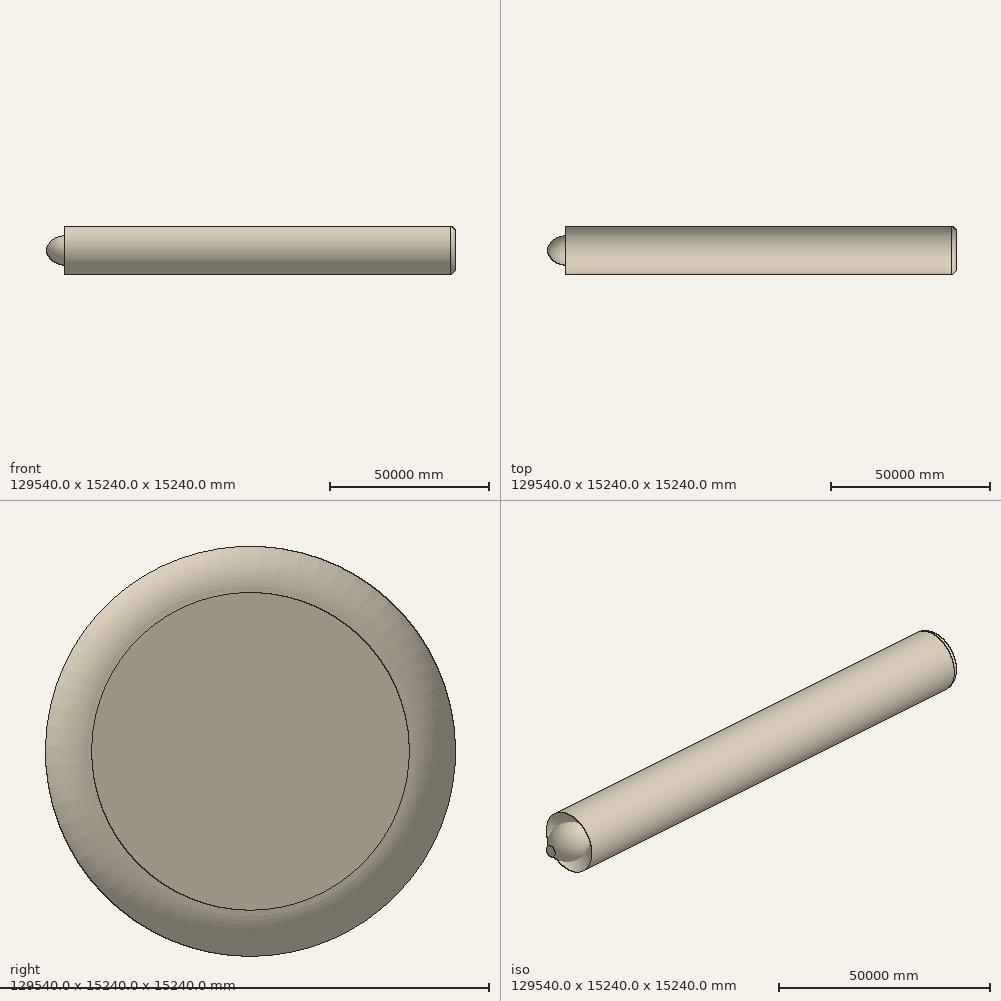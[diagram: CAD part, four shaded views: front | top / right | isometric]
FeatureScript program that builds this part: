
annotation { "Feature Type Name" : "Feature", "Feature Type Description" : "" }
export const myFeature = defineFeature(function(context is Context, id is Id, definition is map)
    precondition{}
    {
        {
            var Q0;
            Q0=qCreatedBy(makeId("Right.planeOp"),FACE);
            var sketch = newSketch(context, id + "F0", { "sketchPlane" : qUnion([Q0])});
            skCircle(sketch, "E0", {"center": v(0, 0) * mm, "radius": 7620 * mm});
            skSolve(sketch);
        }
        {
            var Q0;
            Q0=makeQuery(id+"F0.imprint","IMPRINT",FACE,{"disambiguationData":[TD([[makeQuery(id+"F0.imprint","IMPRINT",EDGE,{"derivedFrom":sQuery(id+"F0.wireOp",EDGE,"E0")}),1.0]])]});
            extrude(context, id + "F1", {"entities" : qUnion([Q0]), "endBound" : BoundingType.SYMMETRIC, "depth" : 129540 * mm, "offsetDistance" : 25.4 * mm});
        }
        {
            var Q0;
            Q0=makeQuery(id+"F1.opExtrude","CAP_EDGE",EDGE,{"disambiguationData":[OSD([sQuery(id+"F0.wireOp",EDGE,"E0")])],"isStart":true});
            fillet(context, id + "F2", {"entities" : qUnion([Q0]), "radius" : 6132.1 * mm, "tangentPropagation" : true, "allowEdgeOverflow" : false});
        }
        {
            var Q0;
            Q0=makeQuery(id+"F1.opExtrude","CAP_FACE",FACE,{"disambiguationData":[OSD([sQuery(id+"F0.wireOp",EDGE,"E0")])],"isStart":false});
            fillet(context, id + "F3", {"entities" : qUnion([Q0]), "radius" : 1717 * mm, "tangentPropagation" : true, "allowEdgeOverflow" : false});
        }
    });
